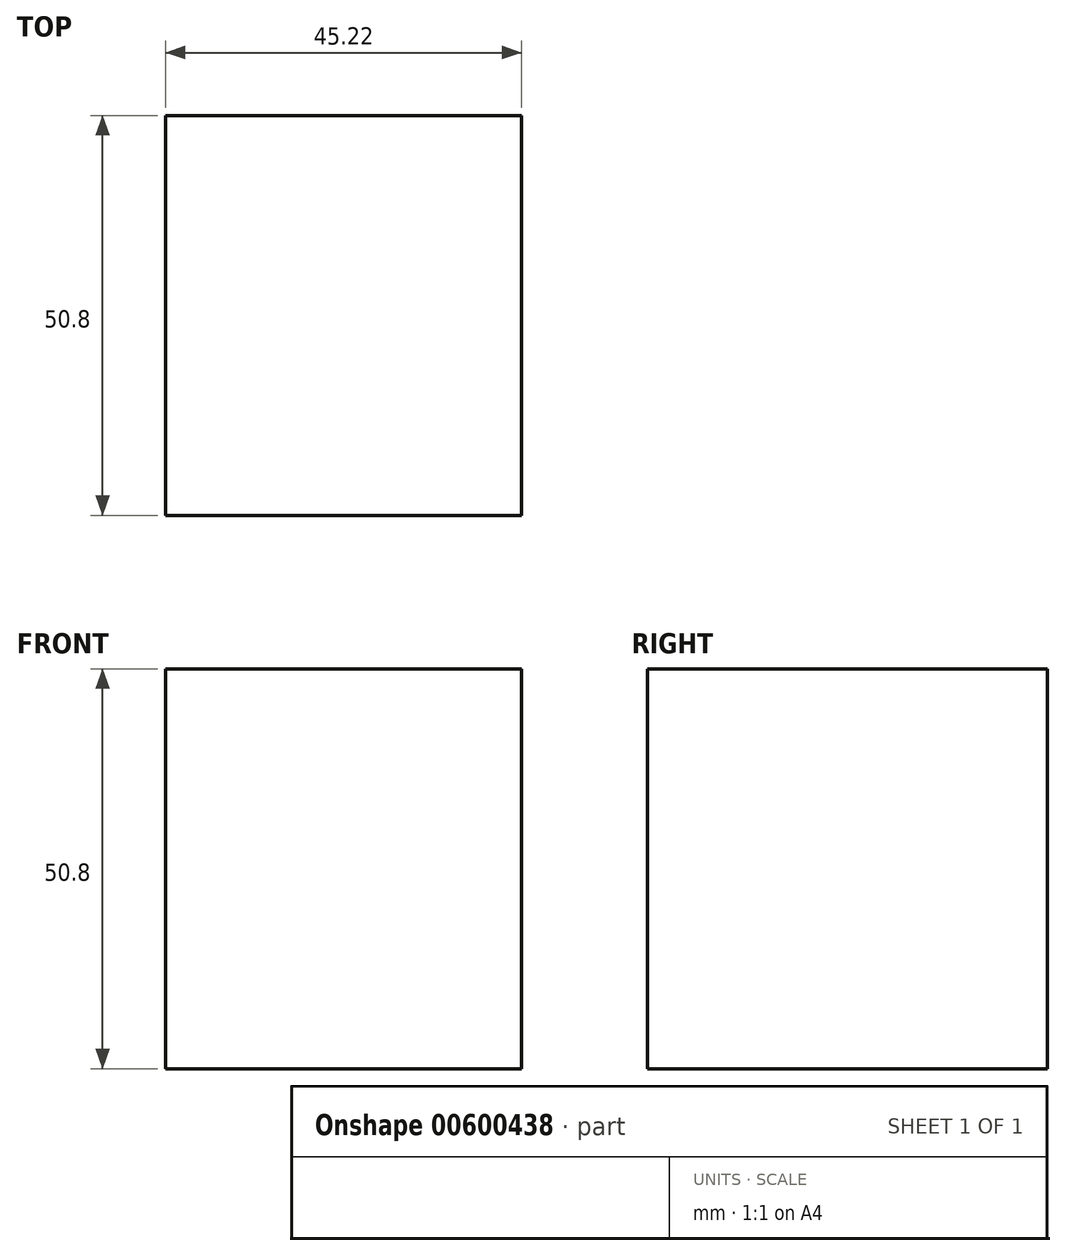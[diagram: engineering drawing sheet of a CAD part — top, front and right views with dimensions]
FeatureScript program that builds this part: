
annotation { "Feature Type Name" : "Feature", "Feature Type Description" : "" }
export const myFeature = defineFeature(function(context is Context, id is Id, definition is map)
    precondition{}
    {
        {
            var Q0;
            Q0=qCreatedBy(makeId("Top.planeOp"),FACE);
            var sketch = newSketch(context, id + "F0", { "sketchPlane" : qUnion([Q0])});
            skLineSegment(sketch, "E0", {"start": v(0, 0) * mm, "end": v(-22.6, 0) * mm});
            skLineSegment(sketch, "E1", {"start": v(0, 0) * mm, "end": v(22.6, 0) * mm});
            skLineSegment(sketch, "E2", {"start": v(22.6, 0) * mm, "end": v(22.6, 50.8) * mm});
            skLineSegment(sketch, "E3", {"start": v(-22.6, 0) * mm, "end": v(-22.6, 50.8) * mm});
            skLineSegment(sketch, "E4", {"start": v(-22.6, 50.8) * mm, "end": v(22.6, 50.8) * mm});
            skSolve(sketch);
        }
        {
            var Q0;
            Q0=makeQuery(id+"F0.imprint","IMPRINT",FACE,{"disambiguationData":[TD([[makeQuery(id+"F0.imprint","IMPRINT",EDGE,{"derivedFrom":sQuery(id+"F0.wireOp",EDGE,"E0")}),-1.0]])]});
            extrude(context, id + "F1", {"entities" : qUnion([Q0]), "depth" : 50.8 * mm, "offsetDistance" : 25.4 * mm});
        }
    });
